# Revit family: G220760JX-012_JBBFX22NMX
name_source: partatom
category: Specialty Equipment
units: mm (PartAtom-declared; Revit-internal decimal feet)

## family parameters
Always vertical = Yes
Cut with Voids When Loaded = No
Enable Cutting in Views = No
Maintain Annotation Orientation = No
Part Type = Normal
Room Calculation Point = No
Round Connector Dimension = Use Diameter
Shared = No
Work Plane-Based = No

## types (1)
- JBBFX22NMX
    Accent Material = ARCAT - Metal - Steel - Stainless
    Apparent Load = 0 VA
    Back Panel Material = ARCAT - Metal - Steel - Black
    Back Strip Material = ARCAT - Metal - Steel - White
    Body Material = ARCAT - Metal - Steel -Stainless
    Button Mat = ARCAT - Rubber-Black
    Clearance Material = ARCAT - Clearance
    Default Elevation = 0 mm  [stored 0 ft]
    Depth = 0 mm  [stored 0 ft]
    Description = 22" Built-In Bottom Mount Refrigerator
    Displey Pannale = ARCAT - Plastic- Grey Light
    Door Front Panel Material = ARCAT - Plastic- Grey Light
    Door Material = ARCAT - Metal - Steel - Stainless - Gray
    Door Rubber Material = ARCAT - Rubber-White
    Family Name = Panel-Ready 22" Built-In Refrigerator
    Feature 1 = Precision Temperature Management™ System
    Feature 2 = Quiet Refrigeration at 31 dBA
    Feature 3 = Fully Flush & Integrated Design
    Handle Material = ARCAT - Metal - Steel - Stainless - Gray
    Height = 69.7 mm
    Hinges Material = ARCAT - Plastic - Dark Gray
    Voltage = 0 V
    Width = 21.9 mm
    Wood paanle = ARCAT - Plastic - Black

note: [stored X ft] marks values corroborated as IEEE doubles in the binary element streams (Revit-internal decimal feet)

## geometry (parser evidence)
native form markers: Sweep x3
no freeform markers — native parametric forms only
